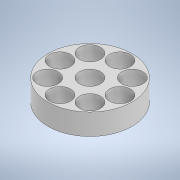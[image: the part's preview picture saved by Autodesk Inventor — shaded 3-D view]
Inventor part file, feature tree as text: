
AUTODESK INVENTOR PART (.ipt)
format: ipt  version: 2022 (Build 260153000, 153)  size: 143,872 bytes
history: native  units: mm
features: extrude x1, sketch x1
ambient origin geometry x8: Origin, YZ Plane, XZ Plane, XY Plane, X Axis, Y Axis, Z Axis, Center Point
bodies: Solid1 (feature_tree)
feature tree (2):
  extrude  "Extrusion1"  Depth=30.0mm
  sketch  "Sketch1"  dims[d0=55.0mm d1=30.0mm d2=80.0mm d4=360.0deg d6=32.0mm d7=30.0mm d8=0.0mm d19=30.0mm d20=0.872665mm d21=0.5mm d22=0.872665mm]
